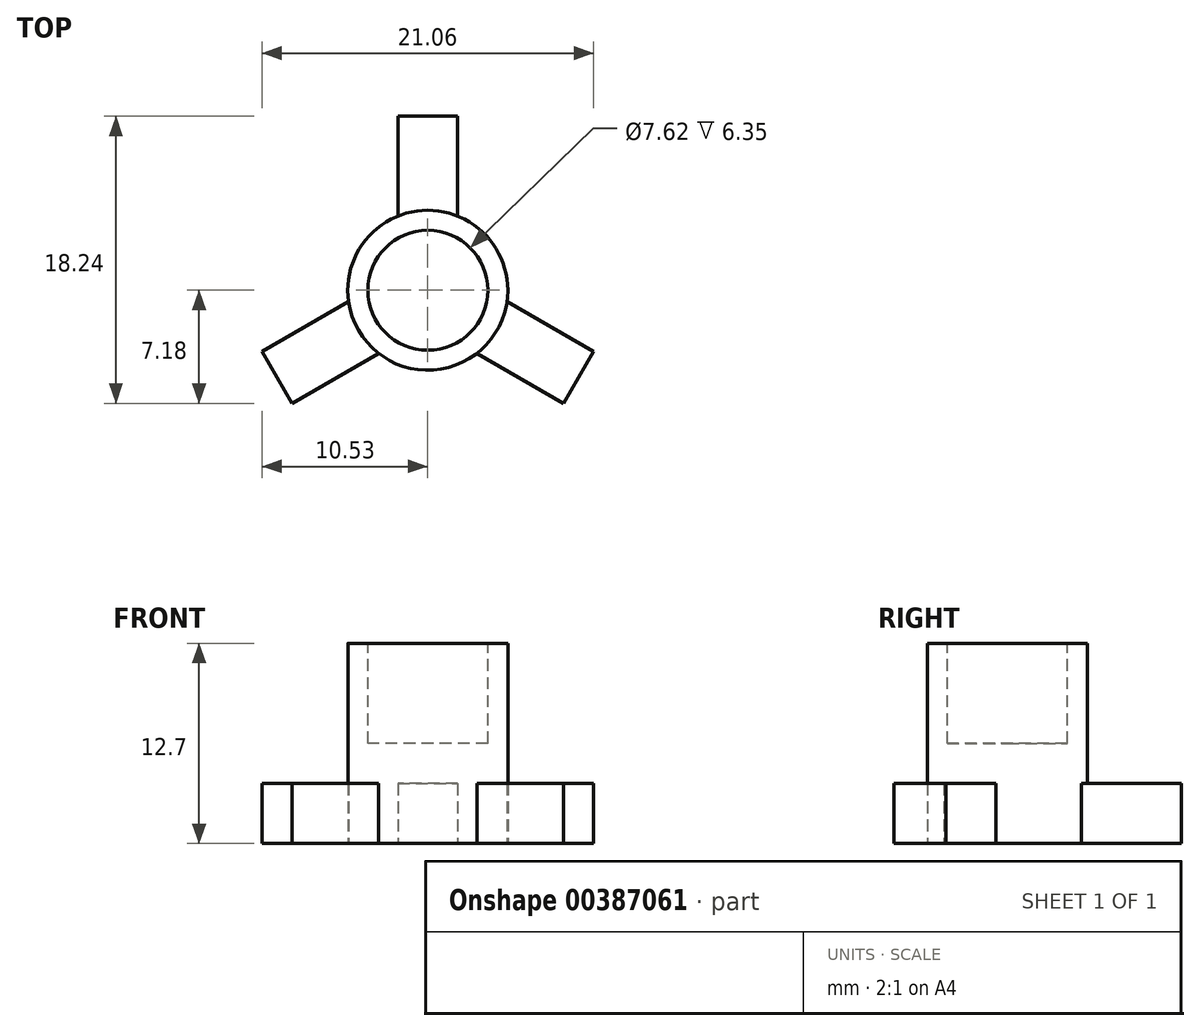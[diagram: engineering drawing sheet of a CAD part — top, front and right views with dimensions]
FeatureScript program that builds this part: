
annotation { "Feature Type Name" : "Feature", "Feature Type Description" : "" }
export const myFeature = defineFeature(function(context is Context, id is Id, definition is map)
    precondition{}
    {
        {
            var Q0;
            Q0=qCreatedBy(makeId("Top.planeOp"),FACE);
            var sketch = newSketch(context, id + "F0", { "sketchPlane" : qUnion([Q0])});
            skCircle(sketch, "E0", {"center": v(0, 0) * mm, "radius": 5.08 * mm});
            skLineSegment(sketch, "E1", {"start": v(-1.9, 4.7) * mm, "end": v(-1.9, 11.06) * mm});
            skLineSegment(sketch, "E2", {"start": v(-1.9, 11.06) * mm, "end": v(1.9, 11.06) * mm});
            skLineSegment(sketch, "E3", {"start": v(1.9, 11.06) * mm, "end": v(1.9, 4.7) * mm});
            skLineSegment(sketch, "E4.1.0", {"start": v(-3.13, -4) * mm, "end": v(-8.63, -7.18) * mm});
            skLineSegment(sketch, "E4.1.1", {"start": v(-8.63, -7.18) * mm, "end": v(-10.53, -3.88) * mm});
            skLineSegment(sketch, "E4.1.2", {"start": v(-10.53, -3.88) * mm, "end": v(-5.03, -0.7) * mm});
            skLineSegment(sketch, "E4.2.0", {"start": v(5.03, -0.7) * mm, "end": v(10.53, -3.88) * mm});
            skLineSegment(sketch, "E4.2.1", {"start": v(10.53, -3.88) * mm, "end": v(8.63, -7.18) * mm});
            skLineSegment(sketch, "E4.2.2", {"start": v(8.63, -7.18) * mm, "end": v(3.13, -4) * mm});
            skSolve(sketch);
        }
        {
            var Q0;
            {var subQ0=sQuery(id+"F0.wireOp",EDGE,"E0");var subQ4=makeQuery(id+"F0.imprint","INTERSECT",VERTEX,{"derivedFrom":[subQ0,sQuery(id+"F0.wireOp",EDGE,"E1")]});Q0=makeQuery(id+"F0.imprint","IMPRINT",FACE,{"disambiguationData":[TD([[makeQuery(id+"F0.imprint","IMPRINT",EDGE,{"disambiguationData":[TD([[subQ4,1.0]])],"derivedFrom":subQ0}),1.0]])]});}
            extrude(context, id + "F1", {"entities" : qUnion([Q0]), "depth" : 12.7 * mm});
        }
        {
            var Q0;
            Q0=qCreatedBy(makeId("Top.planeOp"),FACE);
            var sketch = newSketch(context, id + "F2", { "sketchPlane" : qUnion([Q0])});
            skCircle(sketch, "E5", {"center": v(0, 0) * mm, "radius": 5.08 * mm});
            skLineSegment(sketch, "E6", {"start": v(-1.9, 4.7) * mm, "end": v(-1.9, 11.06) * mm});
            skLineSegment(sketch, "E7", {"start": v(-1.9, 11.06) * mm, "end": v(1.9, 11.06) * mm});
            skLineSegment(sketch, "E8", {"start": v(1.9, 11.06) * mm, "end": v(1.9, 4.7) * mm});
            skLineSegment(sketch, "E9.1.0", {"start": v(-3.13, -4) * mm, "end": v(-8.63, -7.18) * mm});
            skLineSegment(sketch, "E9.1.1", {"start": v(-8.63, -7.18) * mm, "end": v(-10.53, -3.88) * mm});
            skLineSegment(sketch, "E9.1.2", {"start": v(-10.53, -3.88) * mm, "end": v(-5.03, -0.7) * mm});
            skLineSegment(sketch, "E9.2.0", {"start": v(5.03, -0.7) * mm, "end": v(10.53, -3.88) * mm});
            skLineSegment(sketch, "E9.2.1", {"start": v(10.53, -3.88) * mm, "end": v(8.63, -7.18) * mm});
            skLineSegment(sketch, "E9.2.2", {"start": v(8.63, -7.18) * mm, "end": v(3.13, -4) * mm});
            skSolve(sketch);
        }
        {
            var Q0;
            {var subQ0=sQuery(id+"F2.wireOp",EDGE,"E9.2.0");Q0=makeQuery(id+"F2.imprint","IMPRINT",FACE,{"disambiguationData":[TD([[makeQuery(id+"F2.imprint","IMPRINT",EDGE,{"derivedFrom":subQ0}),-1.0]])]});}
            var Q1;
            {var subQ0=sQuery(id+"F2.wireOp",EDGE,"E6");Q1=makeQuery(id+"F2.imprint","IMPRINT",FACE,{"disambiguationData":[TD([[makeQuery(id+"F2.imprint","IMPRINT",EDGE,{"derivedFrom":subQ0}),-1.0]])]});}
            var Q2;
            {var subQ0=sQuery(id+"F2.wireOp",EDGE,"E9.1.0");Q2=makeQuery(id+"F2.imprint","IMPRINT",FACE,{"disambiguationData":[TD([[makeQuery(id+"F2.imprint","IMPRINT",EDGE,{"derivedFrom":subQ0}),-1.0]])]});}
            extrude(context, id + "F3", {"entities" : qUnion([Q0, Q1, Q2]), "operationType" : NewBodyOperationType.ADD, "depth" : 3.8 * mm});
        }
        {
            var Q0;
            Q0=makeQuery(id+"F1.opExtrude","CAP_FACE",FACE,{"disambiguationData":[OSD([sQuery(id+"F0.wireOp",EDGE,"E0")])],"isStart":false});
            var sketch = newSketch(context, id + "F4", { "sketchPlane" : qUnion([Q0])});
            skCircle(sketch, "E10", {"center": v(0, 0) * mm, "radius": 3.81 * mm});
            skSolve(sketch);
        }
        {
            var Q0;
            Q0=makeQuery(id+"F4.imprint","IMPRINT",FACE,{"disambiguationData":[TD([[makeQuery(id+"F4.imprint","IMPRINT",EDGE,{"derivedFrom":sQuery(id+"F4.wireOp",EDGE,"E10")}),1.0]])]});
            extrude(context, id + "F5", {"entities" : qUnion([Q0]), "operationType" : NewBodyOperationType.REMOVE, "oppositeDirection" : true, "depth" : 6.35 * mm});
        }
    });
